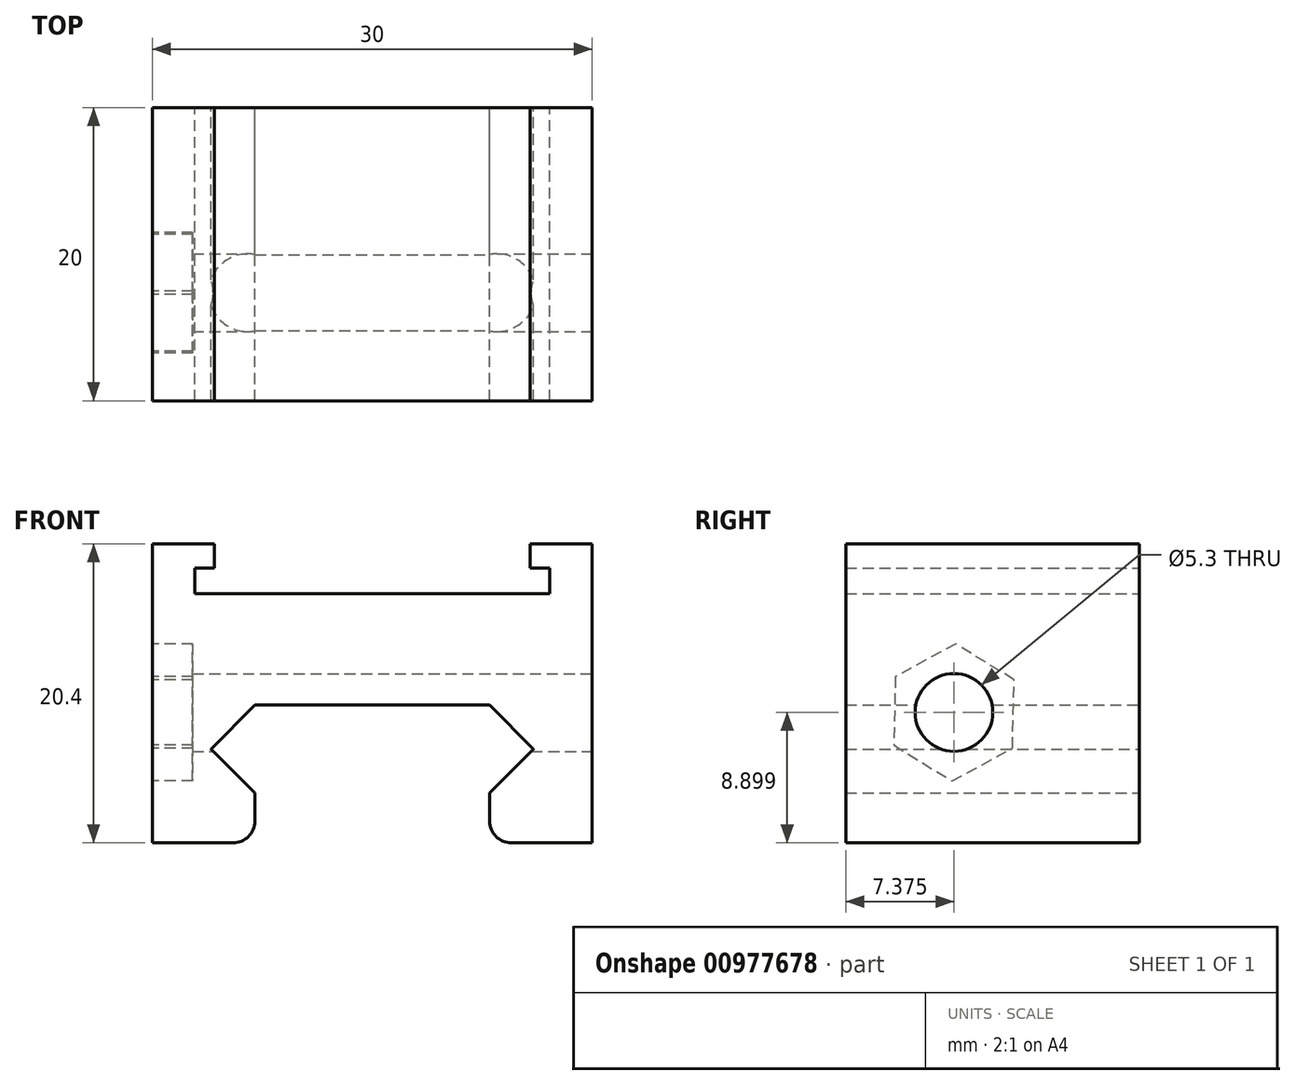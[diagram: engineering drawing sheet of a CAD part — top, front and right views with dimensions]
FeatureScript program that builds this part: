
annotation { "Feature Type Name" : "Feature", "Feature Type Description" : "" }
export const myFeature = defineFeature(function(context is Context, id is Id, definition is map)
    precondition{}
    {
        {
            var Q0;
            Q0=qCreatedBy(makeId("Front.planeOp"),FACE);
            var sketch = newSketch(context, id + "F0", { "sketchPlane" : qUnion([Q0])});
            skLineSegment(sketch, "E0", {"start": v(-12.1, 16.96) * mm, "end": v(12.1, 16.96) * mm});
            skLineSegment(sketch, "E1", {"start": v(12.1, 16.96) * mm, "end": v(12.1, 18.7) * mm});
            skLineSegment(sketch, "E2", {"start": v(12.1, 18.7) * mm, "end": v(10.75, 18.7) * mm});
            skLineSegment(sketch, "E3", {"start": v(10.75, 18.7) * mm, "end": v(10.75, 20.36) * mm});
            skLineSegment(sketch, "E4", {"start": v(10.75, 20.36) * mm, "end": v(15, 20.36) * mm});
            skLineSegment(sketch, "E5", {"start": v(15, 20.36) * mm, "end": v(15, -0.04) * mm});
            skLineSegment(sketch, "E6", {"start": v(15, -0.04) * mm, "end": v(9.5, -0.04) * mm});
            skLineSegment(sketch, "E7", {"start": v(-12.1, 16.96) * mm, "end": v(-12.1, 18.7) * mm});
            skLineSegment(sketch, "E8", {"start": v(-12.1, 18.7) * mm, "end": v(-10.75, 18.7) * mm});
            skLineSegment(sketch, "E9", {"start": v(-10.75, 18.7) * mm, "end": v(-10.75, 20.36) * mm});
            skLineSegment(sketch, "E10", {"start": v(-10.75, 20.36) * mm, "end": v(-15, 20.36) * mm});
            skLineSegment(sketch, "E11", {"start": v(-15, 20.36) * mm, "end": v(-15, -0.04) * mm});
            skLineSegment(sketch, "E12", {"start": v(-15, -0.04) * mm, "end": v(-9.5, -0.04) * mm});
            skLineSegment(sketch, "E13", {"start": v(-11, 6.36) * mm, "end": v(-8, 9.36) * mm});
            skLineSegment(sketch, "E14", {"start": v(-8, 9.36) * mm, "end": v(8, 9.36) * mm});
            skLineSegment(sketch, "E15", {"start": v(8, 9.36) * mm, "end": v(11, 6.36) * mm});
            skLineSegment(sketch, "E16", {"start": v(11, 6.36) * mm, "end": v(8, 3.36) * mm});
            skLineSegment(sketch, "E17", {"start": v(8, 3.36) * mm, "end": v(8, 1.46) * mm});
            skLineSegment(sketch, "E18", {"start": v(-8, 3.36) * mm, "end": v(-8, 1.46) * mm});
            skLineSegment(sketch, "E19", {"start": v(-11, 6.36) * mm, "end": v(-8, 3.36) * mm});
            skArc(sketch, "E20", {"start": v(-8, 1.46) * mm, "mid": v(-8.44, 0.4) * mm, "end": v(-9.5, -0.04) * mm});
            skArc(sketch, "E21", {"start": v(8, 1.46) * mm, "mid": v(8.44, 0.4) * mm, "end": v(9.5, -0.04) * mm});
            skSolve(sketch);
        }
        {
            var Q0;
            Q0=makeQuery(id+"F0.imprint","IMPRINT",FACE,{"disambiguationData":[TD([[makeQuery(id+"F0.imprint","IMPRINT",EDGE,{"derivedFrom":sQuery(id+"F0.wireOp",EDGE,"E0")}),-1.0]])]});
            extrude(context, id + "F1", {"entities" : qUnion([Q0]), "depth" : 20 * mm, "offsetDistance" : 25 * mm});
        }
        {
            var Q0;
            Q0=makeQuery(id+"F1.opExtrude","SWEPT_FACE",FACE,{"disambiguationData":[OSD([sQuery(id+"F0.wireOp",EDGE,"E5")])]});
            var sketch = newSketch(context, id + "F2", { "sketchPlane" : qUnion([Q0])});
            skLineSegment(sketch, "E22", {"start": v(-20, 6.36) * mm, "end": v(0, 6.36) * mm, "construction": true});
            skCircle(sketch, "E23", {"center": v(-12.62, 8.86) * mm, "radius": 2.65 * mm});
            skSolve(sketch);
        }
        {
            var Q0;
            Q0 = qSketchRegion(id + "F2", true);
            extrude(context, id + "F3", {"entities" : qUnion([Q0]), "operationType" : NewBodyOperationType.REMOVE, "oppositeDirection" : true, "depth" : 30 * mm, "offsetDistance" : 25 * mm});
        }
        {
            var Q0;
            Q0=makeQuery(id+"F1.opExtrude","SWEPT_FACE",FACE,{"disambiguationData":[OSD([sQuery(id+"F0.wireOp",EDGE,"E11")])]});
            var sketch = newSketch(context, id + "F4", { "sketchPlane" : qUnion([Q0])});
            skCircle(sketch, "E24.cCircle", {"center": v(12.62, 8.86) * mm, "radius": 4.05 * mm, "construction": true});
            skLineSegment(sketch, "E24.0", {"start": v(12.5, 13.53) * mm, "end": v(16.61, 11.3) * mm});
            skLineSegment(sketch, "E24.1", {"start": v(16.61, 11.3) * mm, "end": v(16.73, 6.63) * mm});
            skLineSegment(sketch, "E24.2", {"start": v(16.73, 6.63) * mm, "end": v(12.75, 4.18) * mm});
            skLineSegment(sketch, "E24.3", {"start": v(12.75, 4.18) * mm, "end": v(8.64, 6.42) * mm});
            skLineSegment(sketch, "E24.4", {"start": v(8.64, 6.42) * mm, "end": v(8.52, 11.1) * mm});
            skLineSegment(sketch, "E24.5", {"start": v(8.52, 11.1) * mm, "end": v(12.5, 13.53) * mm});
            skPoint(sketch, "E24.0.midPoint", {"position": v(14.56, 12.42) * mm});
            skSolve(sketch);
        }
        {
            var Q0;
            Q0 = qSketchRegion(id + "F4", true);
            extrude(context, id + "F5", {"entities" : qUnion([Q0]), "operationType" : NewBodyOperationType.REMOVE, "oppositeDirection" : true, "depth" : 2.75 * mm, "offsetDistance" : 25 * mm});
        }
    });
